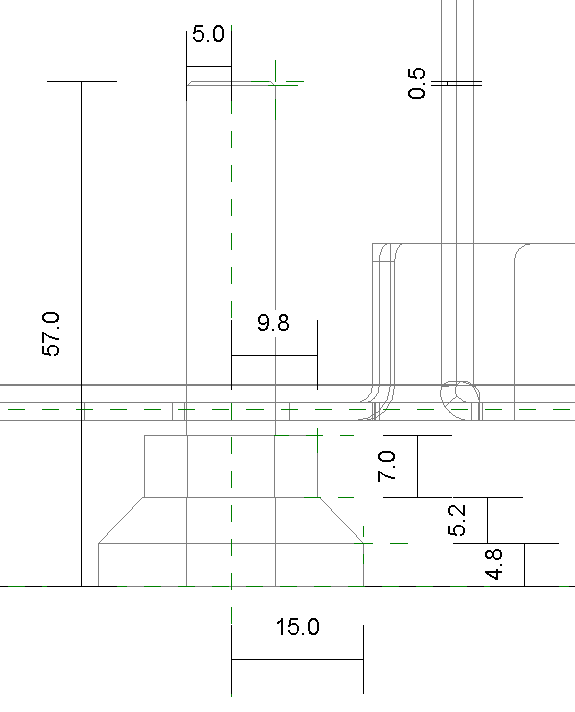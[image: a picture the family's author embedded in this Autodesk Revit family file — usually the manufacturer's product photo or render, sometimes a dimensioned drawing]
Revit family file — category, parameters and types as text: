
# Revit family: Condensinox - depuis 2018-04_FR_B
name_source: partatom
category: Equipement de génie climatique
revit_build: Autodesk Revit 2015 (Build: 20140606_1530(x64)
units: mm (PartAtom-declared; Revit-internal decimal feet)

## types (5) — shared parameters
Classe Nox = 6
Concepteurs = Bim Conseil Formation / HMT International
Distance_Dentretien_avant = 800 mm
Etiquette énergie (disponible sur nos sites) = https://www.atlantic-solutions-chaufferie.fr
Evac a = Non
Evac b = Non
Fabricant = Atlantic Solutions Chaufferie
Famille = Chaudière collective sol gaz
Fréquence (Hz) = 50
Garantie autres pièces = 2
Garantie corps de chauffe (an) = 3
Hauteur_evacuation_condensats = 114 mm  [stored 0.374016 ft]
Hauteur_mini_pieds = 20 mm  [stored 0.0656168 ft]
Hauteur_retour_chaud = 400 mm  [stored 1.31234 ft]
Hauteur_retour_froid = 336 mm  [stored 1.10236 ft]
Lien Page produit = https://www.atlantic-solutions-chaufferie.fr
Lien données RT (Edibatec) = http://www.edibatec.org
Lien fiche Pep = http://register.pep-ecopassport.org
Lien pièces détachées = https://www.atlantic-solutions-chaufferie.fr
Marque3D = Non
Marque_Commerciale = Non
Materiau_carrosserie = Tole_metallisee_bleue
Materiau_porte_tableau_commande = tole_grise_metallisee
Materiau_socle = acier noir
Matériau corps de chauffe = Acier inoxydable
Nom_Commercial = Non
Nombre piquages = 2 ou 3
Pression d'alimentation gaz naturel (mbar) = 20
Pression d'alimentation propane (mbar) = 37
Pression de service (bar) = 4
Raccordement fumées = Cheminée (B23/B23p) et Ventouse (C13/C33/C53)
Réseau (mono/tri) = Monophasé
Taux de modulation (%) = 20
Température de consigne départ maximale (°C) = 80
Tension d'alimentation (V) = 230
Type d'énergie = Gaz naturel ou Propane
URL = https://www.atlantic-solutions-chaufferie.fr
Zone_Dentretien = Non
Ø_nominal_depart = 32 mm  [stored 0.104987 ft]
Ø_nominal_evacuation_condensats = 25 mm  [stored 0.082021 ft]
Ø_nominal_piquage_retour_chaud = 32 mm  [stored 0.104987 ft]
Ø_nominal_piquage_retour_froid = 32 mm  [stored 0.104987 ft]

## per-type parameters (varying)
- 40_kW: Code Article=041600; Debit_Gaz_a_Pn(15°c)_G20/G25=4.4 m³/h; Decalage_lateral_purgeur=269 mm  [stored 0.882546 ft]; Description=Chaudière sol gaz à condensation en inox 40 kW; Distance _Dentretient_LateraleA=200 mm  [stored 0.656168 ft]; Distance-Dentretien_haut=1750 mm; Distance_Dentretien_ArriereC=200 mm  [stored 0.656168 ft]; E=58 mm  [stored 0.190289 ft]; F=100 mm  [stored 0.328084 ft]; Hauteur=1223 mm  [stored 4.01247 ft]; Hauteur_Totale=1494 mm  [stored 4.90157 ft]; Hauteur_afficheur_HMI_IMH=1158 mm  [stored 3.79921 ft]; Hauteur_capot=184 mm; Hauteur_depart=406 mm  [stored 1.33202 ft]; Hauteur_depart_cheminee=1449 mm  [stored 4.75394 ft]; Hauteur_logo_atl=1450 mm  [stored 4.75722 ft]; Hauteur_piquage_gaz=1354 mm  [stored 4.44226 ft]; Largeur=595 mm  [stored 1.9521 ft]; Poids à vide (kg)=134; Position_laterale_logo_atl=550 mm; Position_laterale_piquage_gaz=205 mm  [stored 0.672572 ft]; Position_laterale_piquages=76 mm  [stored 0.249344 ft]; Profondeur=670 mm  [stored 2.19816 ft]; Puissance utile nominale à régime 50/30 °C (kW)=43.8; Puissance utile nominale à régime 80/60 °C (kW)=40; Puissance électrique absorbée à Qn (W)=120; Puissance_nominale=40 kW; Référence=Condensinox 40; Types=40kW : 40Kw; Volume en eau (l)=94 m³; Ø_connexion_tuyau_evacuation_fumee=100 mm  [stored 0.328084 ft]; Ø_nominal_piquage_gaz=15 mm  [stored 0.0492126 ft]; Ø_sortie_fumee=80 mm  [stored 0.262467 ft]
- 80_kW: Code Article=041602; Debit_Gaz_a_Pn(15°c)_G20/G25=8.8 m³/h; Decalage_lateral_purgeur=303 mm  [stored 0.994094 ft]; Description=Chaudière sol gaz à condensation en inox 80 kW; Distance _Dentretient_LateraleA=500 mm  [stored 1.64042 ft]; Distance-Dentretien_haut=1980 mm; Distance_Dentretien_ArriereC=500 mm  [stored 1.64042 ft]; E=102 mm; F=110 mm  [stored 0.360892 ft]; Hauteur=1368 mm  [stored 4.48819 ft]; Hauteur_Totale=1707 mm; Hauteur_afficheur_HMI_IMH=1301 mm  [stored 4.26837 ft]; Hauteur_capot=269 mm  [stored 0.882546 ft]; Hauteur_depart=550 mm; Hauteur_depart_cheminee=1626 mm; Hauteur_logo_atl=1683 mm  [stored 5.52165 ft]; Hauteur_piquage_gaz=1529 mm  [stored 5.0164 ft]; Largeur=695 mm  [stored 2.28018 ft]; Poids à vide (kg)=215; Position_laterale_logo_atl=650 mm  [stored 2.13255 ft]; Position_laterale_piquage_gaz=131 mm  [stored 0.42979 ft]; Position_laterale_piquages=85 mm  [stored 0.278871 ft]; Profondeur=773 mm  [stored 2.53609 ft]; Puissance utile nominale à régime 50/30 °C (kW)=87.5; Puissance utile nominale à régime 80/60 °C (kW)=80; Puissance électrique absorbée à Qn (W)=210; Puissance_nominale=80 kW; Référence=Condensinox 80; Types=80kW : 80Kw; Volume en eau (l)=136 m³; Ø_connexion_tuyau_evacuation_fumee=110 mm  [stored 0.360892 ft]; Ø_nominal_piquage_gaz=20 mm  [stored 0.0656168 ft]; Ø_sortie_fumee=100 mm  [stored 0.328084 ft]
- 60_kW: Code Article=041601; Debit_Gaz_a_Pn(15°c)_G20/G25=6.6 m³/h; Decalage_lateral_purgeur=269 mm  [stored 0.882546 ft]; Description=Chaudière sol gaz à condensation en inox 60 kW; Distance _Dentretient_LateraleA=200 mm  [stored 0.656168 ft]; Distance-Dentretien_haut=1750 mm; Distance_Dentretien_ArriereC=200 mm  [stored 0.656168 ft]; E=58 mm  [stored 0.190289 ft]; F=100 mm  [stored 0.328084 ft]; Hauteur=1223 mm  [stored 4.01247 ft]; Hauteur_Totale=1494 mm  [stored 4.90157 ft]; Hauteur_afficheur_HMI_IMH=1158 mm  [stored 3.79921 ft]; Hauteur_capot=184 mm; Hauteur_depart=406 mm  [stored 1.33202 ft]; Hauteur_depart_cheminee=1449 mm  [stored 4.75394 ft]; Hauteur_logo_atl=1450 mm  [stored 4.75722 ft]; Hauteur_piquage_gaz=1354 mm  [stored 4.44226 ft]; Largeur=595 mm  [stored 1.9521 ft]; Poids à vide (kg)=140; Position_laterale_logo_atl=550 mm; Position_laterale_piquage_gaz=205 mm  [stored 0.672572 ft]; Position_laterale_piquages=76 mm  [stored 0.249344 ft]; Profondeur=670 mm  [stored 2.19816 ft]; Puissance utile nominale à régime 50/30 °C (kW)=65,5; Puissance utile nominale à régime 80/60 °C (kW)=60; Puissance électrique absorbée à Qn (W)=160; Puissance_nominale=60 kW; Référence=Condensinox 60; Types=60kW : 60Kw; Volume en eau (l)=88 m³; Ø_connexion_tuyau_evacuation_fumee=100 mm  [stored 0.328084 ft]; Ø_nominal_piquage_gaz=15 mm  [stored 0.0492126 ft]; Ø_sortie_fumee=80 mm  [stored 0.262467 ft]
- 100_kW: Code Article=041603; Debit_Gaz_a_Pn(15°c)_G20/G25=10.6 m³/h; Decalage_lateral_purgeur=303 mm  [stored 0.994094 ft]; Description=Chaudière sol gaz à condensation en inox 100 kW; Distance _Dentretient_LateraleA=500 mm  [stored 1.64042 ft]; Distance-Dentretien_haut=1980 mm; Distance_Dentretien_ArriereC=500 mm  [stored 1.64042 ft]; E=102 mm; F=110 mm  [stored 0.360892 ft]; Hauteur=1368 mm  [stored 4.48819 ft]; Hauteur_Totale=1707 mm; Hauteur_afficheur_HMI_IMH=1301 mm  [stored 4.26837 ft]; Hauteur_capot=269 mm  [stored 0.882546 ft]; Hauteur_depart=550 mm; Hauteur_depart_cheminee=1626 mm; Hauteur_logo_atl=1683 mm  [stored 5.52165 ft]; Hauteur_piquage_gaz=1529 mm  [stored 5.0164 ft]; Largeur=695 mm  [stored 2.28018 ft]; Poids à vide (kg)=225; Position_laterale_logo_atl=650 mm  [stored 2.13255 ft]; Position_laterale_piquage_gaz=131 mm  [stored 0.42979 ft]; Position_laterale_piquages=85 mm  [stored 0.278871 ft]; Profondeur=773 mm  [stored 2.53609 ft]; Puissance utile nominale à régime 50/30 °C (kW)=105.5; Puissance utile nominale à régime 80/60 °C (kW)=97; Puissance électrique absorbée à Qn (W)=280; Puissance_nominale=100 kW; Référence=Condensinox 100; Types=100kW : 100Kw; Volume en eau (l)=128 m³; Ø_connexion_tuyau_evacuation_fumee=110 mm  [stored 0.360892 ft]; Ø_nominal_piquage_gaz=20 mm  [stored 0.0656168 ft]; Ø_sortie_fumee=100 mm  [stored 0.328084 ft]
- 70_kW: Code Article=041624; Debit_Gaz_a_Pn(15°c)_G20/G25=7.7 m³/h; Decalage_lateral_purgeur=303 mm  [stored 0.994094 ft]; Description=Chaudière sol gaz à condensation en inox 70 kW; Distance _Dentretient_LateraleA=500 mm  [stored 1.64042 ft]; Distance-Dentretien_haut=1980 mm; Distance_Dentretien_ArriereC=500 mm  [stored 1.64042 ft]; E=102 mm; F=110 mm  [stored 0.360892 ft]; Hauteur=1368 mm  [stored 4.48819 ft]; Hauteur_Totale=1707 mm; Hauteur_afficheur_HMI_IMH=1301 mm  [stored 4.26837 ft]; Hauteur_capot=269 mm  [stored 0.882546 ft]; Hauteur_depart=550 mm; Hauteur_depart_cheminee=1626 mm; Hauteur_logo_atl=1683 mm  [stored 5.52165 ft]; Hauteur_piquage_gaz=1529 mm  [stored 5.0164 ft]; Largeur=695 mm  [stored 2.28018 ft]; Poids à vide (kg)=215; Position_laterale_logo_atl=650 mm  [stored 2.13255 ft]; Position_laterale_piquage_gaz=131 mm  [stored 0.42979 ft]; Position_laterale_piquages=85 mm  [stored 0.278871 ft]; Profondeur=773 mm  [stored 2.53609 ft]; Puissance utile nominale à régime 50/30 °C (kW)=76,5; Puissance utile nominale à régime 80/60 °C (kW)=69,9; Puissance électrique absorbée à Qn (W)=210; Puissance_nominale=70 kW; Référence=Condensinox 70; Types=80kW : 80Kw; Volume en eau (l)=136 m³; Ø_connexion_tuyau_evacuation_fumee=110 mm  [stored 0.360892 ft]; Ø_nominal_piquage_gaz=20 mm  [stored 0.0656168 ft]; Ø_sortie_fumee=100 mm  [stored 0.328084 ft]

note: [stored X ft] marks values corroborated as IEEE doubles in the binary element streams (Revit-internal decimal feet)
